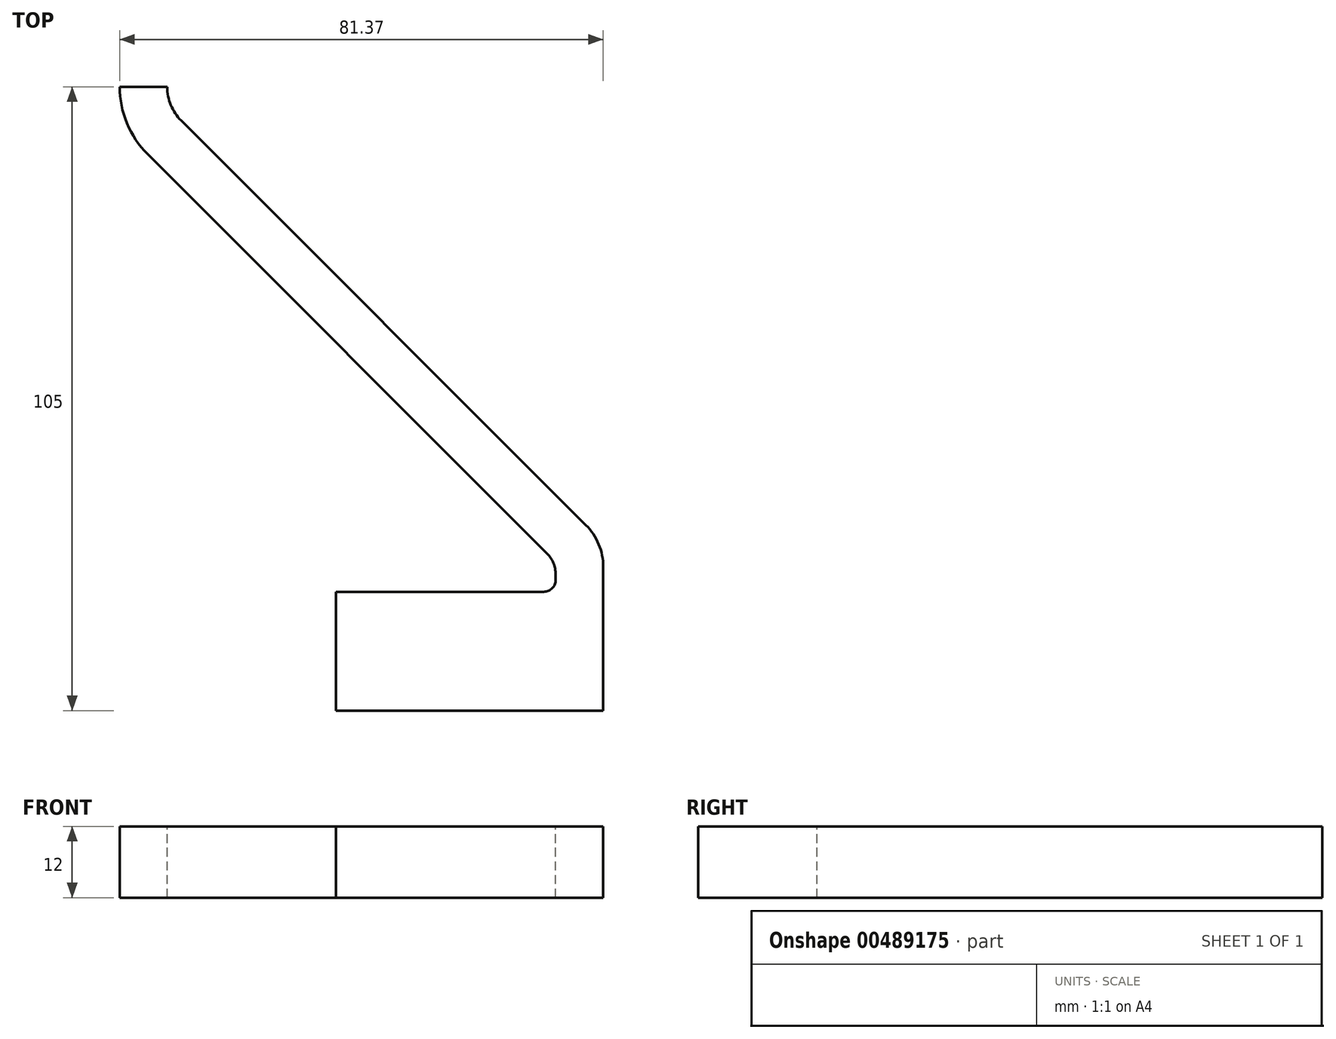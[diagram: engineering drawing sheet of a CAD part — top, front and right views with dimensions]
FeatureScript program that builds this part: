
annotation { "Feature Type Name" : "Feature", "Feature Type Description" : "" }
export const myFeature = defineFeature(function(context is Context, id is Id, definition is map)
    precondition{}
    {
        {
            var Q0;
            Q0=qCreatedBy(makeId("Top.planeOp"),FACE);
            var sketch = newSketch(context, id + "F0", { "sketchPlane" : qUnion([Q0])});
            skLineSegment(sketch, "E0", {"start": v(0, 0) * mm, "end": v(45, 0) * mm});
            skLineSegment(sketch, "E1", {"start": v(45, 0) * mm, "end": v(45, 24.17) * mm});
            skLineSegment(sketch, "E2", {"start": v(42.07, 31.24) * mm, "end": v(-26.03, 99.34) * mm});
            skLineSegment(sketch, "E3", {"start": v(-26.03, 110.66) * mm, "end": v(45, 181.69) * mm});
            skLineSegment(sketch, "E4", {"start": v(0, 0) * mm, "end": v(0, 20) * mm});
            skLineSegment(sketch, "E5", {"start": v(0, 20) * mm, "end": v(35, 20) * mm});
            skLineSegment(sketch, "E6", {"start": v(37, 22) * mm, "end": v(37, 22.93) * mm});
            skLineSegment(sketch, "E7", {"start": v(35.54, 26.46) * mm, "end": v(-31.69, 93.69) * mm});
            skLineSegment(sketch, "E8", {"start": v(-31.69, 116.31) * mm, "end": v(36.96, 184.96) * mm});
            skPoint(sketch, "E9.visualSharp", {"position": v(37, 20) * mm});
            skArc(sketch, "E9.filletArc", {"start": v(35, 20) * mm, "mid": v(36.41, 20.59) * mm, "end": v(37, 22) * mm});
            skPoint(sketch, "E10.visualSharp", {"position": v(37, 25) * mm});
            skArc(sketch, "E10.filletArc", {"start": v(37, 22.93) * mm, "mid": v(36.62, 24.84) * mm, "end": v(35.54, 26.46) * mm});
            skPoint(sketch, "E11.visualSharp", {"position": v(45, 28.31) * mm});
            skArc(sketch, "E11.filletArc", {"start": v(45, 24.17) * mm, "mid": v(44.24, 28) * mm, "end": v(42.07, 31.24) * mm});
            skPoint(sketch, "E12.visualSharp", {"position": v(-43, 105) * mm});
            skArc(sketch, "E12.filletArc", {"start": v(-31.69, 116.31) * mm, "mid": v(-35.15, 111.12) * mm, "end": v(-36.37, 105) * mm});
            skPoint(sketch, "E13.visualSharp", {"position": v(-31.69, 105) * mm});
            skArc(sketch, "E13.filletArc", {"start": v(-26.03, 110.66) * mm, "mid": v(-27.76, 108.06) * mm, "end": v(-28.37, 105) * mm});
            skLineSegment(sketch, "E14", {"start": v(-36.37, 105) * mm, "end": v(-28.37, 105) * mm});
            skArc(sketch, "E15", {"start": v(-28.37, 105) * mm, "mid": v(-27.76, 101.94) * mm, "end": v(-26.03, 99.34) * mm});
            skArc(sketch, "E16", {"start": v(-36.37, 105) * mm, "mid": v(-35.15, 98.88) * mm, "end": v(-31.69, 93.69) * mm});
            skSolve(sketch);
        }
        {
            var Q0;
            Q0=makeQuery(id+"F0.imprint","IMPRINT",FACE,{"disambiguationData":[TD([[makeQuery(id+"F0.imprint","IMPRINT",EDGE,{"derivedFrom":sQuery(id+"F0.wireOp",EDGE,"E0")}),1.0]])]});
            var Q1;
            Q1=sQuery(id+"F0.wireOp",EDGE,"E2");
            var Q2;
            Q2=sQuery(id+"F0.wireOp",EDGE,"E5");
            var Q3;
            Q3=sQuery(id+"F0.wireOp",EDGE,"E7");
            var Q4;
            Q4=sQuery(id+"F0.wireOp",EDGE,"E11.filletArc");
            var Q5;
            Q5=sQuery(id+"F0.wireOp",EDGE,"E9.filletArc");
            var Q6;
            Q6=sQuery(id+"F0.wireOp",EDGE,"E6");
            var Q7;
            Q7=sQuery(id+"F0.wireOp",EDGE,"E10.filletArc");
            var Q8;
            Q8=sQuery(id+"F0.wireOp",EDGE,"E1");
            var Q9;
            Q9=sQuery(id+"F0.wireOp",EDGE,"E15");
            var Q10;
            Q10=sQuery(id+"F0.wireOp",EDGE,"E14");
            var Q11;
            Q11=sQuery(id+"F0.wireOp",EDGE,"E16");
            var Q12;
            Q12=sQuery(id+"F0.wireOp",EDGE,"E4");
            var Q13;
            Q13=sQuery(id+"F0.wireOp",EDGE,"E0");
            extrude(context, id + "F1", {"entities" : qUnion([Q0]), "surfaceEntities" : qUnion([Q1, Q2, Q3, Q4, Q5, Q6, Q7, Q8, Q9, Q10, Q11, Q12, Q13]), "oppositeDirection" : true, "depth" : 12 * mm});
        }
    });
